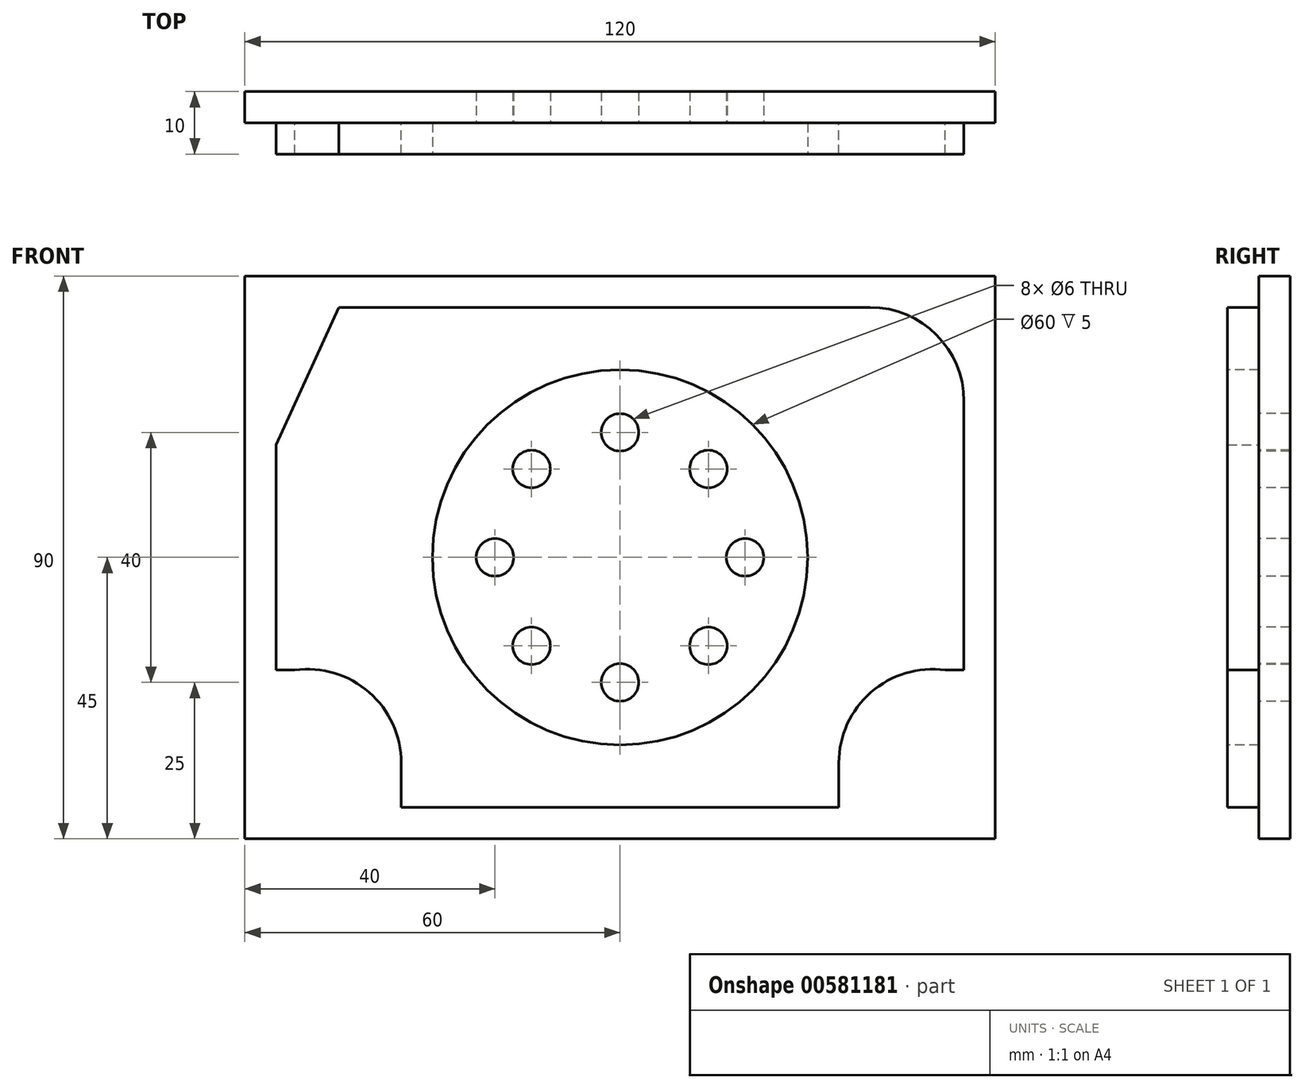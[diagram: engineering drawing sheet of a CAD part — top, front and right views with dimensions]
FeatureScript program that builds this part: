
annotation { "Feature Type Name" : "Feature", "Feature Type Description" : "" }
export const myFeature = defineFeature(function(context is Context, id is Id, definition is map)
    precondition{}
    {
        {
            var Q0;
            Q0=qCreatedBy(makeId("Front.planeOp"),FACE);
            var sketch = newSketch(context, id + "F0", { "sketchPlane" : qUnion([Q0])});
            skLineSegment(sketch, "E0.bottom", {"start": v(60, -45) * mm, "end": v(-60, -45) * mm});
            skLineSegment(sketch, "E0.top", {"start": v(60, 45) * mm, "end": v(-60, 45) * mm});
            skLineSegment(sketch, "E0.left", {"start": v(60, -45) * mm, "end": v(60, 45) * mm});
            skLineSegment(sketch, "E0.right", {"start": v(-60, -45) * mm, "end": v(-60, 45) * mm});
            skPoint(sketch, "E0.middle", {"position": v(0, 0) * mm});
            skSolve(sketch);
        }
        {
            var Q0;
            Q0=makeQuery(id+"F0.imprint","IMPRINT",FACE,{"disambiguationData":[TD([[makeQuery(id+"F0.imprint","IMPRINT",EDGE,{"derivedFrom":sQuery(id+"F0.wireOp",EDGE,"E0.bottom")}),-1.0]])]});
            extrude(context, id + "F1", {"entities" : qUnion([Q0]), "depth" : 5 * mm, "offsetDistance" : 25 * mm});
        }
        {
            var Q0;
            Q0=makeQuery(id+"F1.opExtrude","CAP_FACE",FACE,{"disambiguationData":[OSD([sQuery(id+"F0.wireOp",EDGE,"E0.bottom"),sQuery(id+"F0.wireOp",EDGE,"E0.top"),sQuery(id+"F0.wireOp",EDGE,"E0.left"),sQuery(id+"F0.wireOp",EDGE,"E0.right")])],"isStart":false});
            var sketch = newSketch(context, id + "F2", { "sketchPlane" : qUnion([Q0])});
            skLineSegment(sketch, "E1", {"start": v(-55, 18) * mm, "end": v(-55, -18) * mm});
            skLineSegment(sketch, "E2", {"start": v(-55, 18) * mm, "end": v(-45, 40) * mm});
            skLineSegment(sketch, "E3", {"start": v(-45, 40) * mm, "end": v(40, 40) * mm});
            skLineSegment(sketch, "E4", {"start": v(55, 25) * mm, "end": v(55, -18) * mm});
            skLineSegment(sketch, "E5", {"start": v(-35, -40) * mm, "end": v(35, -40) * mm});
            skPoint(sketch, "E6.visualSharp", {"position": v(55, 40) * mm});
            skArc(sketch, "E6.filletArc", {"start": v(55, 25) * mm, "mid": v(50.6, 35.6) * mm, "end": v(40, 40) * mm});
            skLineSegment(sketch, "E7", {"start": v(-55, -18) * mm, "end": v(-52, -18) * mm});
            skLineSegment(sketch, "E8", {"start": v(-35, -40) * mm, "end": v(-35, -32.87) * mm});
            skArc(sketch, "E9", {"start": v(-35, -32.87) * mm, "mid": v(-40.13, -21.57) * mm, "end": v(-52, -18) * mm});
            skLineSegment(sketch, "E10", {"start": v(55, -18) * mm, "end": v(52, -18) * mm});
            skLineSegment(sketch, "E11", {"start": v(35, -40) * mm, "end": v(35, -32.87) * mm});
            skArc(sketch, "E12", {"start": v(52, -18) * mm, "mid": v(40.13, -21.57) * mm, "end": v(35, -32.87) * mm});
            skSolve(sketch);
        }
        {
            var Q0;
            Q0=makeQuery(id+"F2.imprint","IMPRINT",FACE,{"disambiguationData":[TD([[makeQuery(id+"F2.imprint","IMPRINT",EDGE,{"derivedFrom":sQuery(id+"F2.wireOp",EDGE,"E1")}),1.0]])]});
            extrude(context, id + "F3", {"entities" : qUnion([Q0]), "operationType" : NewBodyOperationType.ADD, "depth" : 5 * mm, "offsetDistance" : 25 * mm});
        }
        {
            var Q0;
            Q0=makeQuery(id+"F3.opExtrude","CAP_FACE",FACE,{"disambiguationData":[OSD([sQuery(id+"F2.wireOp",EDGE,"E1"),sQuery(id+"F2.wireOp",EDGE,"E2"),sQuery(id+"F2.wireOp",EDGE,"E3"),sQuery(id+"F2.wireOp",EDGE,"E4"),sQuery(id+"F2.wireOp",EDGE,"E5"),sQuery(id+"F2.wireOp",EDGE,"5kuEpbX1-WGmx-RCG2-C24u-o4R6bAIocQd1"),sQuery(id+"F2.wireOp",EDGE,"AHOU2zwR-4yOC-SToe-8AJT-hBFkeLSOV56Q")])],"isStart":false});
            var sketch = newSketch(context, id + "F4", { "sketchPlane" : qUnion([Q0])});
            skCircle(sketch, "E13", {"center": v(0, 0) * mm, "radius": 30 * mm});
            skSolve(sketch);
        }
        {
            var Q0;
            Q0=makeQuery(id+"F4.imprint","IMPRINT",FACE,{"disambiguationData":[TD([[makeQuery(id+"F4.imprint","IMPRINT",EDGE,{"derivedFrom":sQuery(id+"F4.wireOp",EDGE,"E13")}),1.0]])]});
            extrude(context, id + "F5", {"entities" : qUnion([Q0]), "operationType" : NewBodyOperationType.REMOVE, "oppositeDirection" : true, "depth" : 5 * mm, "offsetDistance" : 25 * mm});
        }
        {
            var Q0;
            Q0=makeQuery(id+"F5.boolean.opBoolean","COPY",FACE,{"derivedFrom":makeQuery(id+"F5.opExtrude","CAP_FACE",FACE,{"disambiguationData":[OSD([sQuery(id+"F4.wireOp",EDGE,"E13")])],"isStart":false})});
            var sketch = newSketch(context, id + "F6", { "sketchPlane" : qUnion([Q0])});
            skCircle(sketch, "E14", {"center": v(0, 0) * mm, "radius": 20 * mm, "construction": true});
            skCircle(sketch, "E15", {"center": v(0, 20) * mm, "radius": 3 * mm});
            skCircle(sketch, "E16", {"center": v(0, -20) * mm, "radius": 3 * mm});
            skCircle(sketch, "E17", {"center": v(-20, 0) * mm, "radius": 3 * mm});
            skCircle(sketch, "E18", {"center": v(20, 0) * mm, "radius": 3 * mm});
            skCircle(sketch, "E19", {"center": v(14.14, 14.14) * mm, "radius": 3 * mm});
            skCircle(sketch, "E20", {"center": v(-14.14, 14.14) * mm, "radius": 3 * mm});
            skCircle(sketch, "E21", {"center": v(-14.14, -14.14) * mm, "radius": 3 * mm});
            skCircle(sketch, "E22", {"center": v(14.14, -14.14) * mm, "radius": 3 * mm});
            skSolve(sketch);
        }
        {
            var Q0;
            Q0=makeQuery(id+"F6.imprint","IMPRINT",FACE,{"disambiguationData":[TD([[makeQuery(id+"F6.imprint","IMPRINT",EDGE,{"derivedFrom":sQuery(id+"F6.wireOp",EDGE,"E20")}),1.0]])]});
            var Q1;
            Q1=makeQuery(id+"F6.imprint","IMPRINT",FACE,{"disambiguationData":[TD([[makeQuery(id+"F6.imprint","IMPRINT",EDGE,{"derivedFrom":sQuery(id+"F6.wireOp",EDGE,"E15")}),1.0]])]});
            var Q2;
            Q2=makeQuery(id+"F6.imprint","IMPRINT",FACE,{"disambiguationData":[TD([[makeQuery(id+"F6.imprint","IMPRINT",EDGE,{"derivedFrom":sQuery(id+"F6.wireOp",EDGE,"E19")}),1.0]])]});
            var Q3;
            Q3=makeQuery(id+"F6.imprint","IMPRINT",FACE,{"disambiguationData":[TD([[makeQuery(id+"F6.imprint","IMPRINT",EDGE,{"derivedFrom":sQuery(id+"F6.wireOp",EDGE,"E18")}),1.0]])]});
            var Q4;
            Q4=makeQuery(id+"F6.imprint","IMPRINT",FACE,{"disambiguationData":[TD([[makeQuery(id+"F6.imprint","IMPRINT",EDGE,{"derivedFrom":sQuery(id+"F6.wireOp",EDGE,"E22")}),1.0]])]});
            var Q5;
            Q5=makeQuery(id+"F6.imprint","IMPRINT",FACE,{"disambiguationData":[TD([[makeQuery(id+"F6.imprint","IMPRINT",EDGE,{"derivedFrom":sQuery(id+"F6.wireOp",EDGE,"E16")}),1.0]])]});
            var Q6;
            Q6=makeQuery(id+"F6.imprint","IMPRINT",FACE,{"disambiguationData":[TD([[makeQuery(id+"F6.imprint","IMPRINT",EDGE,{"derivedFrom":sQuery(id+"F6.wireOp",EDGE,"E21")}),1.0]])]});
            var Q7;
            Q7=makeQuery(id+"F6.imprint","IMPRINT",FACE,{"disambiguationData":[TD([[makeQuery(id+"F6.imprint","IMPRINT",EDGE,{"derivedFrom":sQuery(id+"F6.wireOp",EDGE,"E17")}),1.0]])]});
            extrude(context, id + "F7", {"entities" : qUnion([Q0, Q1, Q2, Q3, Q4, Q5, Q6, Q7]), "operationType" : NewBodyOperationType.REMOVE, "oppositeDirection" : true, "depth" : 5 * mm, "offsetDistance" : 25 * mm});
        }
    });
